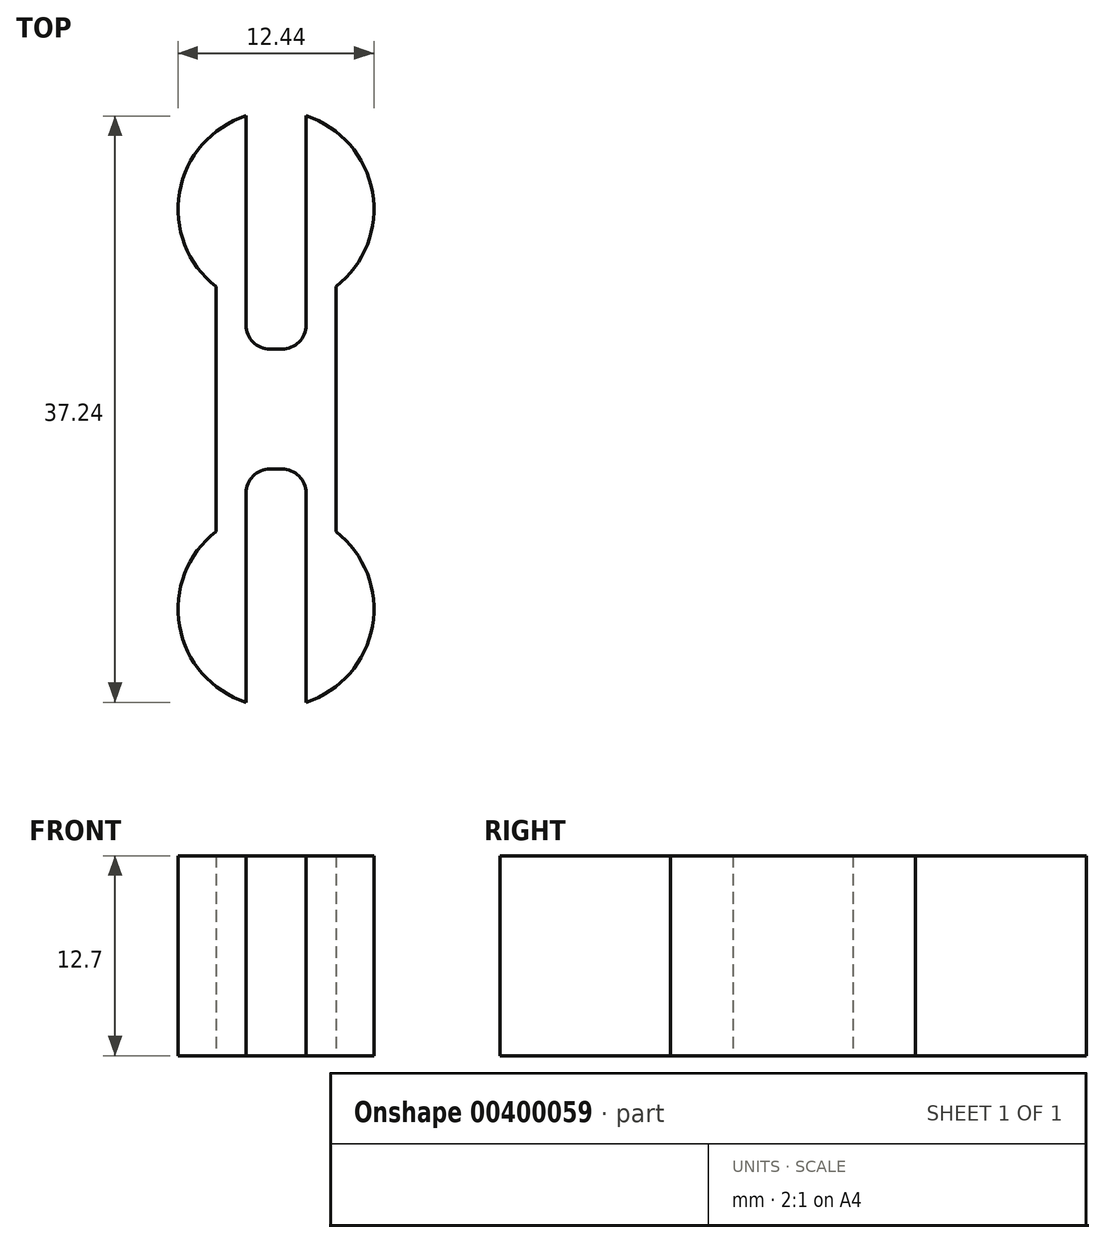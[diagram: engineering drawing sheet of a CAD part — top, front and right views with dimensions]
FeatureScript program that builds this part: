
annotation { "Feature Type Name" : "Feature", "Feature Type Description" : "" }
export const myFeature = defineFeature(function(context is Context, id is Id, definition is map)
    precondition{}
    {
        {
            var Q0;
            Q0=qCreatedBy(makeId("Top.planeOp"),FACE);
            var sketch = newSketch(context, id + "F0", { "sketchPlane" : qUnion([Q0])});
            skLineSegment(sketch, "E0", {"start": v(-3.81, -7.78) * mm, "end": v(-3.81, 7.78) * mm});
            skLineSegment(sketch, "E1", {"start": v(3.81, -7.78) * mm, "end": v(3.81, 7.78) * mm});
            skLineSegment(sketch, "E2", {"start": v(0, 0) * mm, "end": v(0, 23.3) * mm, "construction": true});
            skArc(sketch, "E3", {"start": v(3.81, 7.78) * mm, "mid": v(0, 18.92) * mm, "end": v(-3.81, 7.78) * mm});
            skArc(sketch, "E4", {"start": v(-3.81, -7.78) * mm, "mid": v(0, -18.92) * mm, "end": v(3.81, -7.78) * mm});
            skLineSegment(sketch, "E5", {"start": v(0, 0) * mm, "end": v(-22.44, 0) * mm, "construction": true});
            skSolve(sketch);
        }
        {
            var Q0;
            Q0 = qSketchRegion(id + "F0", true);
            extrude(context, id + "F1", {"entities" : qUnion([Q0]), "depth" : 12.7 * mm});
        }
        {
            var Q0;
            Q0=makeQuery(id+"F1.opExtrude","CAP_FACE",FACE,{"disambiguationData":[OSD([sQuery(id+"F0.wireOp",EDGE,"E0"),sQuery(id+"F0.wireOp",EDGE,"E1"),sQuery(id+"F0.wireOp",EDGE,"E3"),sQuery(id+"F0.wireOp",EDGE,"E4")])],"isStart":true});
            var sketch = newSketch(context, id + "F2", { "sketchPlane" : qUnion([Q0])});
            skLineSegment(sketch, "E6.bottom", {"start": v(1.9, -3.81) * mm, "end": v(-1.9, -3.81) * mm});
            skLineSegment(sketch, "E6.top", {"start": v(1.9, -29.49) * mm, "end": v(-1.9, -29.49) * mm});
            skLineSegment(sketch, "E6.left", {"start": v(1.9, -3.81) * mm, "end": v(1.9, -29.49) * mm});
            skLineSegment(sketch, "E6.right", {"start": v(-1.9, -3.81) * mm, "end": v(-1.9, -29.49) * mm});
            skLineSegment(sketch, "E7", {"start": v(0, 0) * mm, "end": v(0, -17.58) * mm, "construction": true});
            skLineSegment(sketch, "E8", {"start": v(0, 0) * mm, "end": v(14.44, 0) * mm, "construction": true});
            skLineSegment(sketch, "E9.MirrorCS", {"start": v(1.9, 3.81) * mm, "end": v(-1.9, 3.81) * mm});
            skLineSegment(sketch, "E10.MirrorCS", {"start": v(-1.9, 3.8) * mm, "end": v(-1.9, 29.49) * mm});
            skLineSegment(sketch, "E11.MirrorCS", {"start": v(1.9, 29.49) * mm, "end": v(-1.9, 29.49) * mm});
            skLineSegment(sketch, "E12.MirrorCS", {"start": v(1.9, 3.81) * mm, "end": v(1.9, 29.49) * mm});
            skSolve(sketch);
        }
        {
            var Q0;
            Q0 = qSketchRegion(id + "F2", true);
            extrude(context, id + "F3", {"entities" : qUnion([Q0]), "operationType" : NewBodyOperationType.REMOVE, "oppositeDirection" : true, "depth" : 25.4 * mm});
        }
        {
            var Q0;
            Q0=makeQuery(id+"F3.boolean.opBoolean","COPY",EDGE,{"derivedFrom":makeQuery(id+"F3.opExtrude","SWEPT_EDGE",EDGE,{"disambiguationData":[OSD([sQuery(id+"F2.wireOp",EDGE,"E6.bottom"),sQuery(id+"F2.wireOp",EDGE,"E6.left")])]})});
            var Q1;
            Q1=makeQuery(id+"F3.boolean.opBoolean","COPY",EDGE,{"derivedFrom":makeQuery(id+"F3.opExtrude","SWEPT_EDGE",EDGE,{"disambiguationData":[OSD([sQuery(id+"F2.wireOp",EDGE,"E6.bottom"),sQuery(id+"F2.wireOp",EDGE,"E6.right")])]})});
            var Q2;
            Q2=makeQuery(id+"F3.boolean.opBoolean","COPY",EDGE,{"derivedFrom":makeQuery(id+"F3.opExtrude","SWEPT_EDGE",EDGE,{"disambiguationData":[OSD([sQuery(id+"F2.wireOp",EDGE,"E9.MirrorCS"),sQuery(id+"F2.wireOp",EDGE,"E12.MirrorCS")])]})});
            var Q3;
            Q3=makeQuery(id+"F3.boolean.opBoolean","COPY",EDGE,{"derivedFrom":makeQuery(id+"F3.opExtrude","SWEPT_EDGE",EDGE,{"disambiguationData":[OSD([sQuery(id+"F2.wireOp",EDGE,"E9.MirrorCS"),sQuery(id+"F2.wireOp",EDGE,"E10.MirrorCS")])]})});
            fillet(context, id + "F4", {"entities" : qUnion([Q0, Q1, Q2, Q3]), "radius" : 1.52 * mm, "tangentPropagation" : true, "allowEdgeOverflow" : false});
        }
    });
